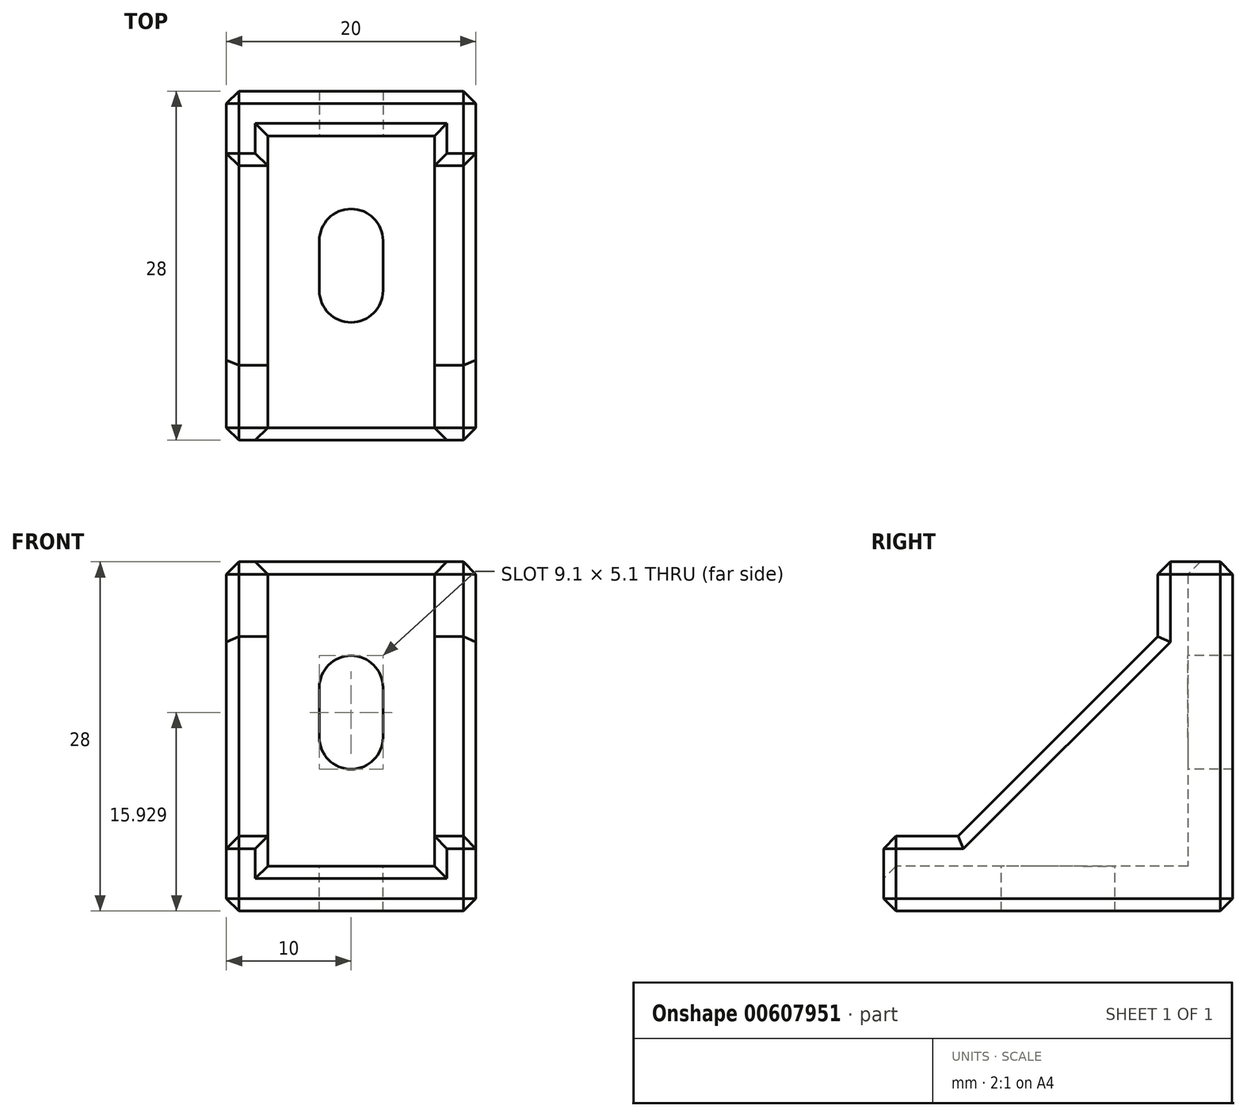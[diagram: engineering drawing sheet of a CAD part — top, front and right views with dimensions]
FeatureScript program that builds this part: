
annotation { "Feature Type Name" : "Feature", "Feature Type Description" : "" }
export const myFeature = defineFeature(function(context is Context, id is Id, definition is map)
    precondition{}
    {
        {
            var Q0;
            Q0=qCreatedBy(makeId("Top.planeOp"),FACE);
            var sketch = newSketch(context, id + "F0", { "sketchPlane" : qUnion([Q0])});
            skLineSegment(sketch, "E0.rect.bottom", {"start": v(10, 14) * mm, "end": v(-10, 14) * mm});
            skLineSegment(sketch, "E0.rect.top", {"start": v(10, -14) * mm, "end": v(-10, -14) * mm});
            skLineSegment(sketch, "E0.rect.left", {"start": v(10, 14) * mm, "end": v(10, -14) * mm});
            skLineSegment(sketch, "E0.rect.right", {"start": v(-10, 14) * mm, "end": v(-10, -14) * mm});
            skPoint(sketch, "E0.rect.middle", {"position": v(0, 0) * mm});
            skSolve(sketch);
        }
        {
            var Q0;
            Q0=makeQuery(id+"F0.imprint","IMPRINT",FACE,{"disambiguationData":[TD([[makeQuery(id+"F0.imprint","IMPRINT",EDGE,{"derivedFrom":sQuery(id+"F0.wireOp",EDGE,"E0.rect.bottom")}),1.0]])]});
            extrude(context, id + "F1", {"entities" : qUnion([Q0]), "depth" : 3.6 * mm});
        }
        {
            var Q0;
            Q0=makeQuery(id+"F1.opExtrude","CAP_FACE",FACE,{"disambiguationData":[OSD([sQuery(id+"F0.wireOp",EDGE,"E0.rect.bottom"),sQuery(id+"F0.wireOp",EDGE,"E0.rect.top"),sQuery(id+"F0.wireOp",EDGE,"E0.rect.left"),sQuery(id+"F0.wireOp",EDGE,"E0.rect.right")])],"isStart":false});
            var sketch = newSketch(context, id + "F2", { "sketchPlane" : qUnion([Q0])});
            skLineSegment(sketch, "E1", {"start": v(6.7, 10.4) * mm, "end": v(-6.7, 10.4) * mm});
            skLineSegment(sketch, "E2", {"start": v(-6.7, 10.4) * mm, "end": v(-6.7, -14) * mm});
            skLineSegment(sketch, "E3", {"start": v(6.69, 10.4) * mm, "end": v(6.69, -14) * mm});
            skLineSegment(sketch, "E4", {"start": v(6.69, -14) * mm, "end": v(10, -14) * mm});
            skLineSegment(sketch, "E5", {"start": v(10, -14) * mm, "end": v(10, 14) * mm});
            skLineSegment(sketch, "E6", {"start": v(10, 14) * mm, "end": v(-10, 14) * mm});
            skLineSegment(sketch, "E7", {"start": v(-10, 14) * mm, "end": v(-10, -14) * mm});
            skLineSegment(sketch, "E8", {"start": v(-10, -14) * mm, "end": v(-6.7, -14) * mm});
            skSolve(sketch);
        }
        {
            var Q0;
            Q0=makeQuery(id+"F2.imprint","IMPRINT",FACE,{"disambiguationData":[TD([[makeQuery(id+"F2.imprint","IMPRINT",EDGE,{"derivedFrom":sQuery(id+"F2.wireOp",EDGE,"E1")}),-1.0]])]});
            extrude(context, id + "F3", {"entities" : qUnion([Q0]), "operationType" : NewBodyOperationType.ADD, "depth" : 28 * mm - 3.6 * mm});
        }
        {
            var Q0;
            Q0=makeQuery(id+"F3.boolean.opBoolean","MERGE",FACE,{"derivedFrom":[makeQuery(id+"F1.opExtrude","SWEPT_FACE",FACE,{"disambiguationData":[OSD([sQuery(id+"F0.wireOp",EDGE,"E0.rect.left")])]}),makeQuery(id+"F3.opExtrude","SWEPT_FACE",FACE,{"disambiguationData":[OSD([sQuery(id+"F2.wireOp",EDGE,"E5")])]})]});
            var sketch = newSketch(context, id + "F4", { "sketchPlane" : qUnion([Q0])});
            skLineSegment(sketch, "E9", {"start": v(-14, 0) * mm, "end": v(-14, 6) * mm});
            skLineSegment(sketch, "E10", {"start": v(-14, 6) * mm, "end": v(-8, 6) * mm});
            skLineSegment(sketch, "E11", {"start": v(-8, 6) * mm, "end": v(8, 22) * mm});
            skLineSegment(sketch, "E12", {"start": v(8, 22) * mm, "end": v(8, 28) * mm});
            skLineSegment(sketch, "E13", {"start": v(8, 28) * mm, "end": v(14, 28) * mm});
            skLineSegment(sketch, "E14", {"start": v(14, 28) * mm, "end": v(14, 0) * mm});
            skLineSegment(sketch, "E15", {"start": v(14, 0) * mm, "end": v(-14, 0) * mm});
            skLineSegment(sketch, "E16", {"start": v(-14, 6) * mm, "end": v(-14, 0) * mm});
            skSolve(sketch);
        }
        {
            var Q0;
            Q0=qSketchRegion(id+"F4",true);
            extrude(context, id + "F5", {"entities" : qUnion([Q0]), "operationType" : NewBodyOperationType.INTERSECT, "oppositeDirection" : true, "depth" : 25 * mm});
        }
        {
            var Q0;
            Q0=makeQuery(id+"F1.opExtrude","CAP_FACE",FACE,{"disambiguationData":[OSD([sQuery(id+"F0.wireOp",EDGE,"E0.rect.bottom"),sQuery(id+"F0.wireOp",EDGE,"E0.rect.top"),sQuery(id+"F0.wireOp",EDGE,"E0.rect.left"),sQuery(id+"F0.wireOp",EDGE,"E0.rect.right")])],"isStart":false});
            var sketch = newSketch(context, id + "F6", { "sketchPlane" : qUnion([Q0])});
            skLineSegment(sketch, "E17.rect.bottom", {"start": v(-2.55, 2) * mm, "end": v(2.55, 2) * mm});
            skLineSegment(sketch, "E17.rect.top", {"start": v(-2.55, -2) * mm, "end": v(2.55, -2) * mm});
            skLineSegment(sketch, "E17.rect.left", {"start": v(-2.55, 2) * mm, "end": v(-2.55, -2) * mm});
            skLineSegment(sketch, "E17.rect.right", {"start": v(2.55, 2) * mm, "end": v(2.55, -2) * mm});
            skPoint(sketch, "E17.rect.middle", {"position": v(0, 0) * mm});
            skArc(sketch, "E18", {"start": v(-2.55, -2) * mm, "mid": v(0, -4.55) * mm, "end": v(2.55, -2) * mm});
            skArc(sketch, "E19", {"start": v(2.55, 2) * mm, "mid": v(0, 4.55) * mm, "end": v(-2.55, 2) * mm});
            skSolve(sketch);
        }
        {
            var Q0;
            Q0=qSketchRegion(id+"F6",true);
            extrude(context, id + "F7", {"entities" : qUnion([Q0]), "operationType" : NewBodyOperationType.REMOVE, "oppositeDirection" : true, "depth" : 25 * mm});
        }
        {
            var Q0;
            Q0=makeQuery(id+"F3.opExtrude","SWEPT_FACE",FACE,{"disambiguationData":[OSD([sQuery(id+"F2.wireOp",EDGE,"E1")])]});
            var sketch = newSketch(context, id + "F8", { "sketchPlane" : qUnion([Q0])});
            skLineSegment(sketch, "E20.rect.bottom", {"start": v(2.55, 13.93) * mm, "end": v(-2.55, 13.93) * mm});
            skLineSegment(sketch, "E20.rect.top", {"start": v(2.55, 17.93) * mm, "end": v(-2.55, 17.93) * mm});
            skLineSegment(sketch, "E20.rect.left", {"start": v(2.55, 13.93) * mm, "end": v(2.55, 17.93) * mm});
            skLineSegment(sketch, "E20.rect.right", {"start": v(-2.55, 13.93) * mm, "end": v(-2.55, 17.93) * mm});
            skPoint(sketch, "E20.rect.middle", {"position": v(0, 15.93) * mm});
            skArc(sketch, "E21", {"start": v(-2.55, 13.93) * mm, "mid": v(0, 11.38) * mm, "end": v(2.55, 13.93) * mm});
            skArc(sketch, "E22", {"start": v(2.55, 17.93) * mm, "mid": v(0, 20.48) * mm, "end": v(-2.55, 17.93) * mm});
            skSolve(sketch);
        }
        {
            var Q0;
            Q0=qSketchRegion(id+"F8",true);
            extrude(context, id + "F9", {"entities" : qUnion([Q0]), "operationType" : NewBodyOperationType.REMOVE, "oppositeDirection" : true, "depth" : 25 * mm});
        }
        {
            var Q0;
            Q0=makeQuery(id+"F1.opExtrude","CAP_EDGE",EDGE,{"disambiguationData":[OSD([sQuery(id+"F0.wireOp",EDGE,"E0.rect.top")])],"isStart":false});
            var Q1;
            Q1=makeQuery(id+"F3.opExtrude","CAP_EDGE",EDGE,{"disambiguationData":[OSD([sQuery(id+"F2.wireOp",EDGE,"E1")])],"isStart":false});
            var Q2;
            Q2=makeQuery(id+"F3.opExtrude","CAP_EDGE",EDGE,{"disambiguationData":[OSD([sQuery(id+"F2.wireOp",EDGE,"E3")])],"isStart":false});
            var Q3;
            Q3=makeQuery(id+"F5.boolean.opBoolean","INTERSECT",EDGE,{"derivedFrom":[makeQuery(id+"F3.opExtrude","SWEPT_FACE",FACE,{"disambiguationData":[OSD([sQuery(id+"F2.wireOp",EDGE,"E3")])]}),makeQuery(id+"F5.boolean.toolComplement.opBoolean","COPY",FACE,{"derivedFrom":makeQuery(id+"F5.opExtrude","SWEPT_FACE",FACE,{"disambiguationData":[OSD([sQuery(id+"F4.wireOp",EDGE,"E12")])]})})]});
            var Q4;
            Q4=makeQuery(id+"F3.opExtrude","CAP_EDGE",EDGE,{"disambiguationData":[OSD([sQuery(id+"F2.wireOp",EDGE,"E2")])],"isStart":false});
            var Q5;
            Q5=makeQuery(id+"F5.boolean.opBoolean","INTERSECT",EDGE,{"derivedFrom":[makeQuery(id+"F3.opExtrude","SWEPT_FACE",FACE,{"disambiguationData":[OSD([sQuery(id+"F2.wireOp",EDGE,"E2")])]}),makeQuery(id+"F5.boolean.toolComplement.opBoolean","COPY",FACE,{"derivedFrom":makeQuery(id+"F5.opExtrude","SWEPT_FACE",FACE,{"disambiguationData":[OSD([sQuery(id+"F4.wireOp",EDGE,"E12")])]})})]});
            var Q6;
            {var subQ0=sQuery(id+"F4.wireOp",EDGE,"E11");var subQ1=sQuery(id+"F4.wireOp",EDGE,"E12");Q6=makeQuery(id+"F5.boolean.opBoolean","COPY",EDGE,{"disambiguationData":[TD([makeQuery(id+"F1.opExtrude","SWEPT_FACE",FACE,{"disambiguationData":[OSD([sQuery(id+"F0.wireOp",EDGE,"E0.rect.right")])]})])],"derivedFrom":makeQuery(id+"F5.boolean.toolComplement.opBoolean","COPY",EDGE,{"derivedFrom":makeQuery(id+"F5.opExtrude","SWEPT_EDGE",EDGE,{"disambiguationData":[OSD([subQ0,subQ1])]})})});}
            var Q7;
            {var subQ0=sQuery(id+"F4.wireOp",EDGE,"E11");var subQ1=sQuery(id+"F4.wireOp",EDGE,"E12");Q7=makeQuery(id+"F5.boolean.opBoolean","COPY",EDGE,{"disambiguationData":[TD([makeQuery(id+"F1.opExtrude","SWEPT_FACE",FACE,{"disambiguationData":[OSD([sQuery(id+"F0.wireOp",EDGE,"E0.rect.left")])]})])],"derivedFrom":makeQuery(id+"F5.boolean.toolComplement.opBoolean","COPY",EDGE,{"derivedFrom":makeQuery(id+"F5.opExtrude","SWEPT_EDGE",EDGE,{"disambiguationData":[OSD([subQ0,subQ1])]})})});}
            var Q8;
            {var subQ2=sQuery(id+"F2.wireOp",EDGE,"E5");var subQ3=sQuery(id+"F4.wireOp",EDGE,"E12");Q8=makeQuery(id+"F5.boolean.opBoolean","COPY",EDGE,{"disambiguationData":[TD([makeQuery(id+"F1.opExtrude","SWEPT_FACE",FACE,{"disambiguationData":[OSD([sQuery(id+"F0.wireOp",EDGE,"E0.rect.right")])]})])],"derivedFrom":makeQuery(id+"F5.boolean.toolComplement.opBoolean","COPY",EDGE,{"derivedFrom":makeQuery(id+"F5.opExtrude","SWEPT_EDGE",EDGE,{"disambiguationData":[OSD([subQ2,subQ3,sQuery(id+"F4.wireOp",EDGE,"E13")])]})})});}
            var Q9;
            {var subQ1=sQuery(id+"F2.wireOp",EDGE,"E5");var subQ2=sQuery(id+"F4.wireOp",EDGE,"E12");Q9=makeQuery(id+"F5.boolean.opBoolean","COPY",EDGE,{"disambiguationData":[TD([makeQuery(id+"F1.opExtrude","SWEPT_FACE",FACE,{"disambiguationData":[OSD([sQuery(id+"F0.wireOp",EDGE,"E0.rect.left")])]})])],"derivedFrom":makeQuery(id+"F5.boolean.toolComplement.opBoolean","COPY",EDGE,{"derivedFrom":makeQuery(id+"F5.opExtrude","SWEPT_EDGE",EDGE,{"disambiguationData":[OSD([subQ1,subQ2,sQuery(id+"F4.wireOp",EDGE,"E13")])]})})});}
            var Q10;
            Q10=makeQuery(id+"F5.boolean.opBoolean","COPY",EDGE,{"derivedFrom":makeQuery(id+"F5.boolean.toolComplement.opBoolean","COPY",EDGE,{"derivedFrom":makeQuery(id+"F5.opExtrude","CAP_EDGE",EDGE,{"disambiguationData":[OSD([sQuery(id+"F4.wireOp",EDGE,"E12")])],"isStart":true})})});
            var Q11;
            Q11=makeQuery(id+"F5.boolean.opBoolean","INTERSECT",EDGE,{"derivedFrom":[makeQuery(id+"F3.boolean.opBoolean","MERGE",FACE,{"derivedFrom":[makeQuery(id+"F1.opExtrude","SWEPT_FACE",FACE,{"disambiguationData":[OSD([sQuery(id+"F0.wireOp",EDGE,"E0.rect.right")])]}),makeQuery(id+"F3.opExtrude","SWEPT_FACE",FACE,{"disambiguationData":[OSD([sQuery(id+"F2.wireOp",EDGE,"E7")])]})]}),makeQuery(id+"F5.boolean.toolComplement.opBoolean","COPY",FACE,{"derivedFrom":makeQuery(id+"F5.opExtrude","SWEPT_FACE",FACE,{"disambiguationData":[OSD([sQuery(id+"F4.wireOp",EDGE,"E12")])]})})]});
            var Q12;
            Q12=makeQuery(id+"F5.boolean.opBoolean","INTERSECT",EDGE,{"derivedFrom":[makeQuery(id+"F3.opExtrude","SWEPT_FACE",FACE,{"disambiguationData":[OSD([sQuery(id+"F2.wireOp",EDGE,"E3")])]}),makeQuery(id+"F5.boolean.toolComplement.opBoolean","COPY",FACE,{"derivedFrom":makeQuery(id+"F5.opExtrude","SWEPT_FACE",FACE,{"disambiguationData":[OSD([sQuery(id+"F4.wireOp",EDGE,"E10")])]})})]});
            var Q13;
            Q13=makeQuery(id+"F5.boolean.opBoolean","COPY",FACE,{"disambiguationData":[TD([makeQuery(id+"F1.opExtrude","SWEPT_FACE",FACE,{"disambiguationData":[OSD([sQuery(id+"F0.wireOp",EDGE,"E0.rect.left")])]})])],"derivedFrom":makeQuery(id+"F5.boolean.toolComplement.opBoolean","COPY",FACE,{"derivedFrom":makeQuery(id+"F5.opExtrude","SWEPT_FACE",FACE,{"disambiguationData":[OSD([sQuery(id+"F4.wireOp",EDGE,"E10")])]})})});
            var Q14;
            Q14=makeQuery(id+"F5.boolean.opBoolean","COPY",FACE,{"disambiguationData":[TD([makeQuery(id+"F1.opExtrude","SWEPT_FACE",FACE,{"disambiguationData":[OSD([sQuery(id+"F0.wireOp",EDGE,"E0.rect.right")])]})])],"derivedFrom":makeQuery(id+"F5.boolean.toolComplement.opBoolean","COPY",FACE,{"derivedFrom":makeQuery(id+"F5.opExtrude","SWEPT_FACE",FACE,{"disambiguationData":[OSD([sQuery(id+"F4.wireOp",EDGE,"E10")])]})})});
            var Q15;
            Q15=makeQuery(id+"F3.boolean.opBoolean","MERGE",FACE,{"derivedFrom":[makeQuery(id+"F1.opExtrude","SWEPT_FACE",FACE,{"disambiguationData":[OSD([sQuery(id+"F0.wireOp",EDGE,"E0.rect.top")])]}),makeQuery(id+"F3.opExtrude","SWEPT_FACE",FACE,{"disambiguationData":[OSD([sQuery(id+"F2.wireOp",EDGE,"E4")])]}),makeQuery(id+"F3.opExtrude","SWEPT_FACE",FACE,{"disambiguationData":[OSD([sQuery(id+"F2.wireOp",EDGE,"E8")])]})]});
            var Q16;
            Q16=makeQuery(id+"F3.opExtrude","CAP_FACE",FACE,{"disambiguationData":[OSD([sQuery(id+"F2.wireOp",EDGE,"E1"),sQuery(id+"F2.wireOp",EDGE,"E2"),sQuery(id+"F2.wireOp",EDGE,"E3"),sQuery(id+"F2.wireOp",EDGE,"E4"),sQuery(id+"F2.wireOp",EDGE,"E5"),sQuery(id+"F2.wireOp",EDGE,"E6"),sQuery(id+"F2.wireOp",EDGE,"E7"),sQuery(id+"F2.wireOp",EDGE,"E8")])],"isStart":false});
            var Q17;
            Q17=makeQuery(id+"F3.boolean.opBoolean","MERGE",FACE,{"derivedFrom":[makeQuery(id+"F1.opExtrude","SWEPT_FACE",FACE,{"disambiguationData":[OSD([sQuery(id+"F0.wireOp",EDGE,"E0.rect.right")])]}),makeQuery(id+"F3.opExtrude","SWEPT_FACE",FACE,{"disambiguationData":[OSD([sQuery(id+"F2.wireOp",EDGE,"E7")])]})]});
            var Q18;
            Q18=makeQuery(id+"F3.boolean.opBoolean","MERGE",FACE,{"derivedFrom":[makeQuery(id+"F1.opExtrude","SWEPT_FACE",FACE,{"disambiguationData":[OSD([sQuery(id+"F0.wireOp",EDGE,"E0.rect.left")])]}),makeQuery(id+"F3.opExtrude","SWEPT_FACE",FACE,{"disambiguationData":[OSD([sQuery(id+"F2.wireOp",EDGE,"E5")])]})]});
            var Q19;
            Q19=makeQuery(id+"F1.opExtrude","CAP_EDGE",EDGE,{"disambiguationData":[OSD([sQuery(id+"F0.wireOp",EDGE,"E0.rect.bottom")])],"isStart":true});
            chamfer(context, id + "F10", {"entities" : qUnion([Q0, Q1, Q2, Q3, Q4, Q5, Q6, Q7, Q8, Q9, Q10, Q11, Q12, Q13, Q14, Q15, Q16, Q17, Q18, Q19]), "width" : 1 * mm, "tangentPropagation" : true});
        }
    });
